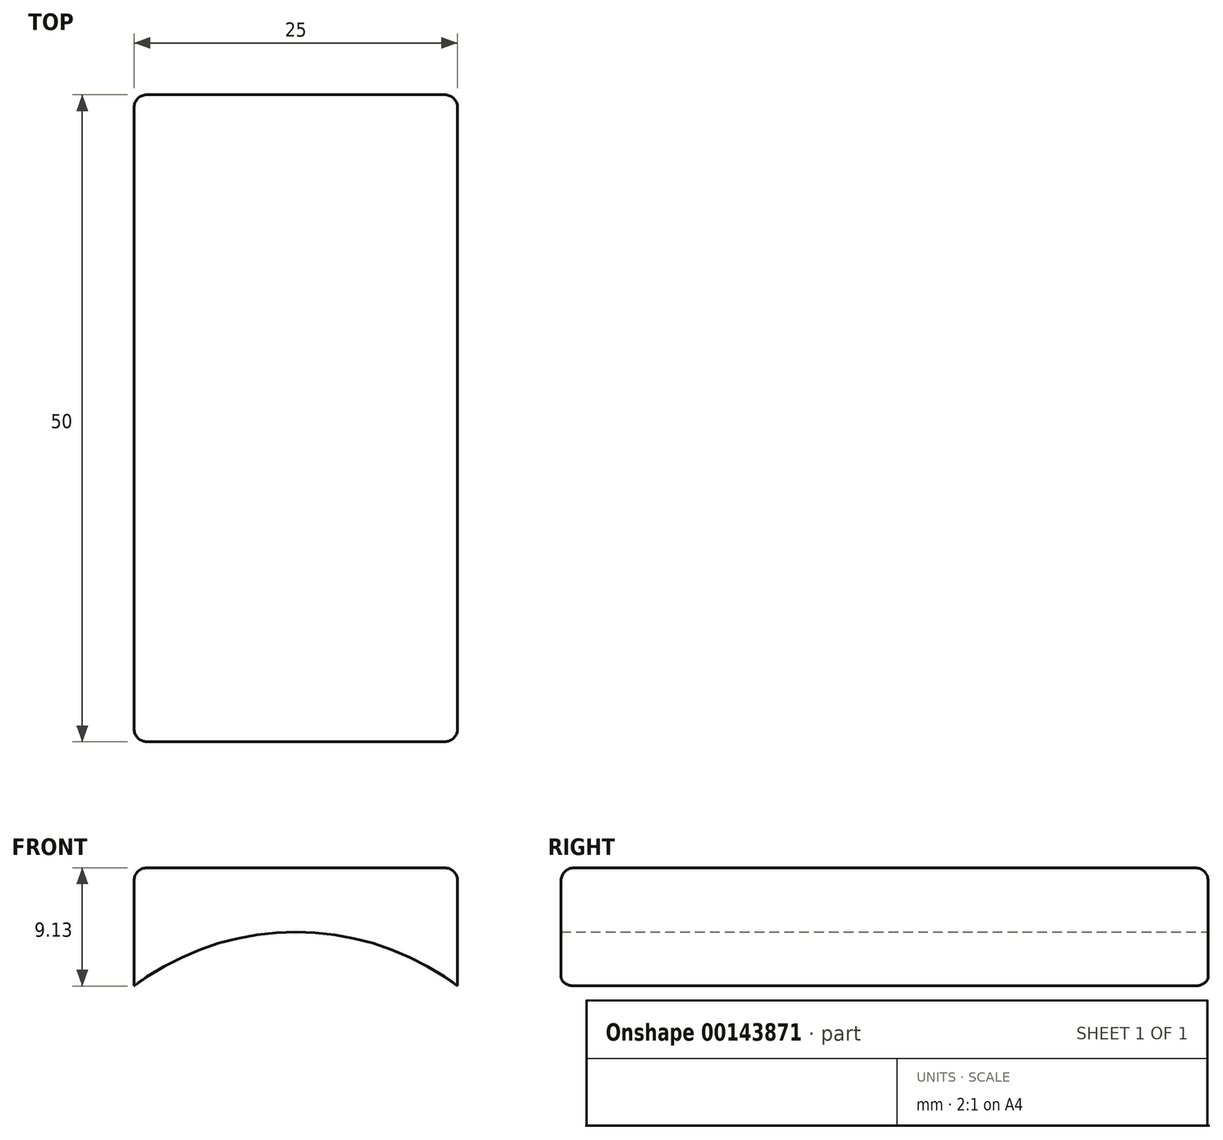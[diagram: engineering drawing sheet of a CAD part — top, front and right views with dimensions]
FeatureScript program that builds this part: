
annotation { "Feature Type Name" : "Feature", "Feature Type Description" : "" }
export const myFeature = defineFeature(function(context is Context, id is Id, definition is map)
    precondition{}
    {
        {
            var Q0;
            Q0=qCreatedBy(makeId("Front.planeOp"),FACE);
            var sketch = newSketch(context, id + "F0", { "sketchPlane" : qUnion([Q0])});
            skLineSegment(sketch, "E0", {"start": v(-12.5, 26) * mm, "end": v(12.5, 26) * mm});
            skLineSegment(sketch, "E1", {"start": v(-12.5, 26) * mm, "end": v(-12.5, 16.87) * mm});
            skLineSegment(sketch, "E2", {"start": v(12.5, 26) * mm, "end": v(12.5, 16.87) * mm});
            skArc(sketch, "E3", {"start": v(12.5, 16.87) * mm, "mid": v(0, 21.04) * mm, "end": v(-12.5, 16.87) * mm});
            skSolve(sketch);
        }
        {
            var Q0;
            Q0=makeQuery(id+"F0.imprint","IMPRINT",FACE,{"disambiguationData":[TD([[makeQuery(id+"F0.imprint","IMPRINT",EDGE,{"derivedFrom":sQuery(id+"F0.wireOp",EDGE,"E0")}),-1.0]])]});
            extrude(context, id + "F1", {"entities" : qUnion([Q0]), "depth" : 50 * mm, "offsetDistance" : 25 * mm});
        }
        {
            var Q0;
            Q0=makeQuery(id+"F1.opExtrude","SWEPT_FACE",FACE,{"disambiguationData":[OSD([sQuery(id+"F0.wireOp",EDGE,"E0")])]});
            var Q1;
            Q1=makeQuery(id+"F1.opExtrude","CAP_EDGE",EDGE,{"disambiguationData":[OSD([sQuery(id+"F0.wireOp",EDGE,"E2")])],"isStart":false});
            var Q2;
            Q2=makeQuery(id+"F1.opExtrude","CAP_EDGE",EDGE,{"disambiguationData":[OSD([sQuery(id+"F0.wireOp",EDGE,"E1")])],"isStart":false});
            var Q3;
            Q3=makeQuery(id+"F1.opExtrude","CAP_EDGE",EDGE,{"disambiguationData":[OSD([sQuery(id+"F0.wireOp",EDGE,"E1")])],"isStart":true});
            var Q4;
            Q4=makeQuery(id+"F1.opExtrude","CAP_EDGE",EDGE,{"disambiguationData":[OSD([sQuery(id+"F0.wireOp",EDGE,"E2")])],"isStart":true});
            fillet(context, id + "F2", {"entities" : qUnion([Q0, Q1, Q2, Q3, Q4]), "radius" : 1 * mm, "tangentPropagation" : true, "allowEdgeOverflow" : false});
        }
    });
